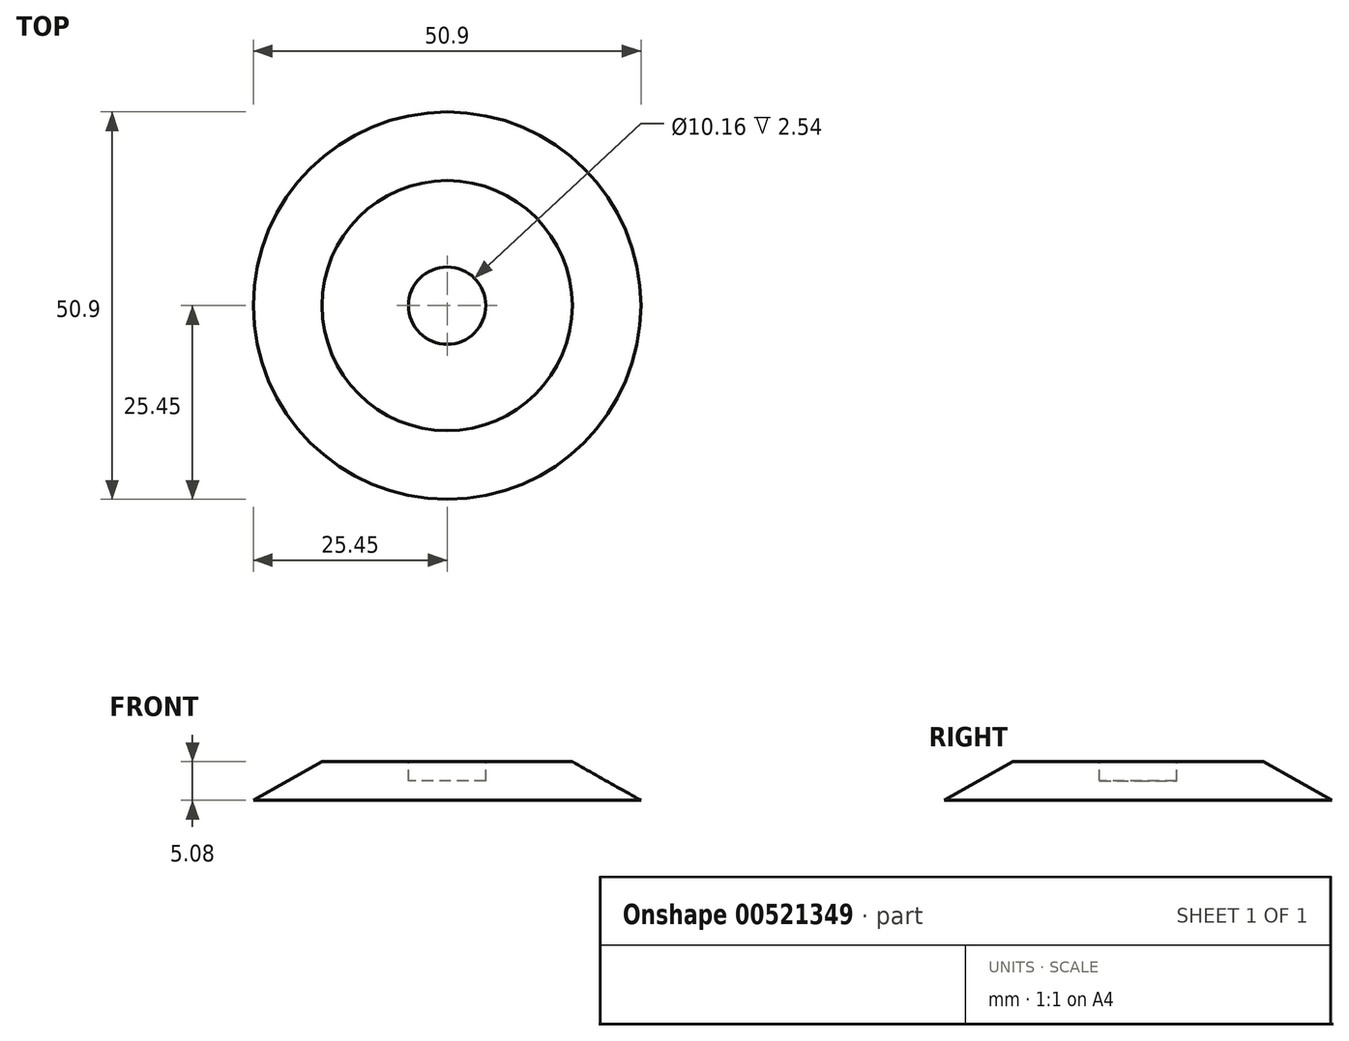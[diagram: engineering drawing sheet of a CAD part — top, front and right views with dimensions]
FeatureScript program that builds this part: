
annotation { "Feature Type Name" : "Feature", "Feature Type Description" : "" }
export const myFeature = defineFeature(function(context is Context, id is Id, definition is map)
    precondition{}
    {
        {
            var Q0;
            Q0=qCreatedBy(makeId("Top.planeOp"),FACE);
            var sketch = newSketch(context, id + "F0", { "sketchPlane" : qUnion([Q0])});
            skCircle(sketch, "E0", {"center": v(0, 0) * mm, "radius": 25.45 * mm});
            skSolve(sketch);
        }
        {
            var Q0;
            Q0=qCreatedBy(makeId("Top.planeOp"),FACE);
            cPlane(context, id + "F1", {"entities" : qUnion([Q0]), "cplaneType" : CPlaneType.OFFSET, "offset" : 5.08 * mm, "width" : 152.4 * mm, "height" : 152.4 * mm});
        }
        {
            var Q0;
            Q0=qCreatedBy(id+"F1.planeOp",FACE);
            var sketch = newSketch(context, id + "F2", { "sketchPlane" : qUnion([Q0])});
            skCircle(sketch, "E1", {"center": v(0, 0) * mm, "radius": 16.44 * mm});
            skSolve(sketch);
        }
        {
            var Q0;
            Q0=makeQuery(id+"F0.imprint","IMPRINT",FACE,{"disambiguationData":[TD([[makeQuery(id+"F0.imprint","IMPRINT",EDGE,{"derivedFrom":sQuery(id+"F0.wireOp",EDGE,"E0")}),1.0]])]});
            var Q1;
            Q1=makeQuery(id+"F2.imprint","IMPRINT",FACE,{"disambiguationData":[TD([[makeQuery(id+"F2.imprint","IMPRINT",EDGE,{"derivedFrom":sQuery(id+"F2.wireOp",EDGE,"E1")}),1.0]])]});
            loft(context, id + "F3", {"sheetProfilesArray" : [{ "sheetProfileEntities" : qUnion([Q0]) }, { "sheetProfileEntities" : qUnion([Q1]) }]});
        }
        {
            var Q0;
            Q0=makeQuery(id+"F3.opLoft","CAP_FACE",FACE,{"disambiguationData":[OSD([makeQuery(id+"F2.imprint","IMPRINT",FACE,{"disambiguationData":[TD([[makeQuery(id+"F2.imprint","IMPRINT",EDGE,{"derivedFrom":sQuery(id+"F2.wireOp",EDGE,"E1")}),1.0]])]})])],"isStart":true});
            var sketch = newSketch(context, id + "F4", { "sketchPlane" : qUnion([Q0])});
            skCircle(sketch, "E2", {"center": v(0, 0) * mm, "radius": 5.08 * mm});
            skSolve(sketch);
        }
        {
            var Q0;
            Q0 = qSketchRegion(id + "F4", true);
            extrude(context, id + "F5", {"entities" : qUnion([Q0]), "operationType" : NewBodyOperationType.REMOVE, "oppositeDirection" : true, "depth" : 2.54 * mm, "offsetDistance" : 25.4 * mm});
        }
    });
